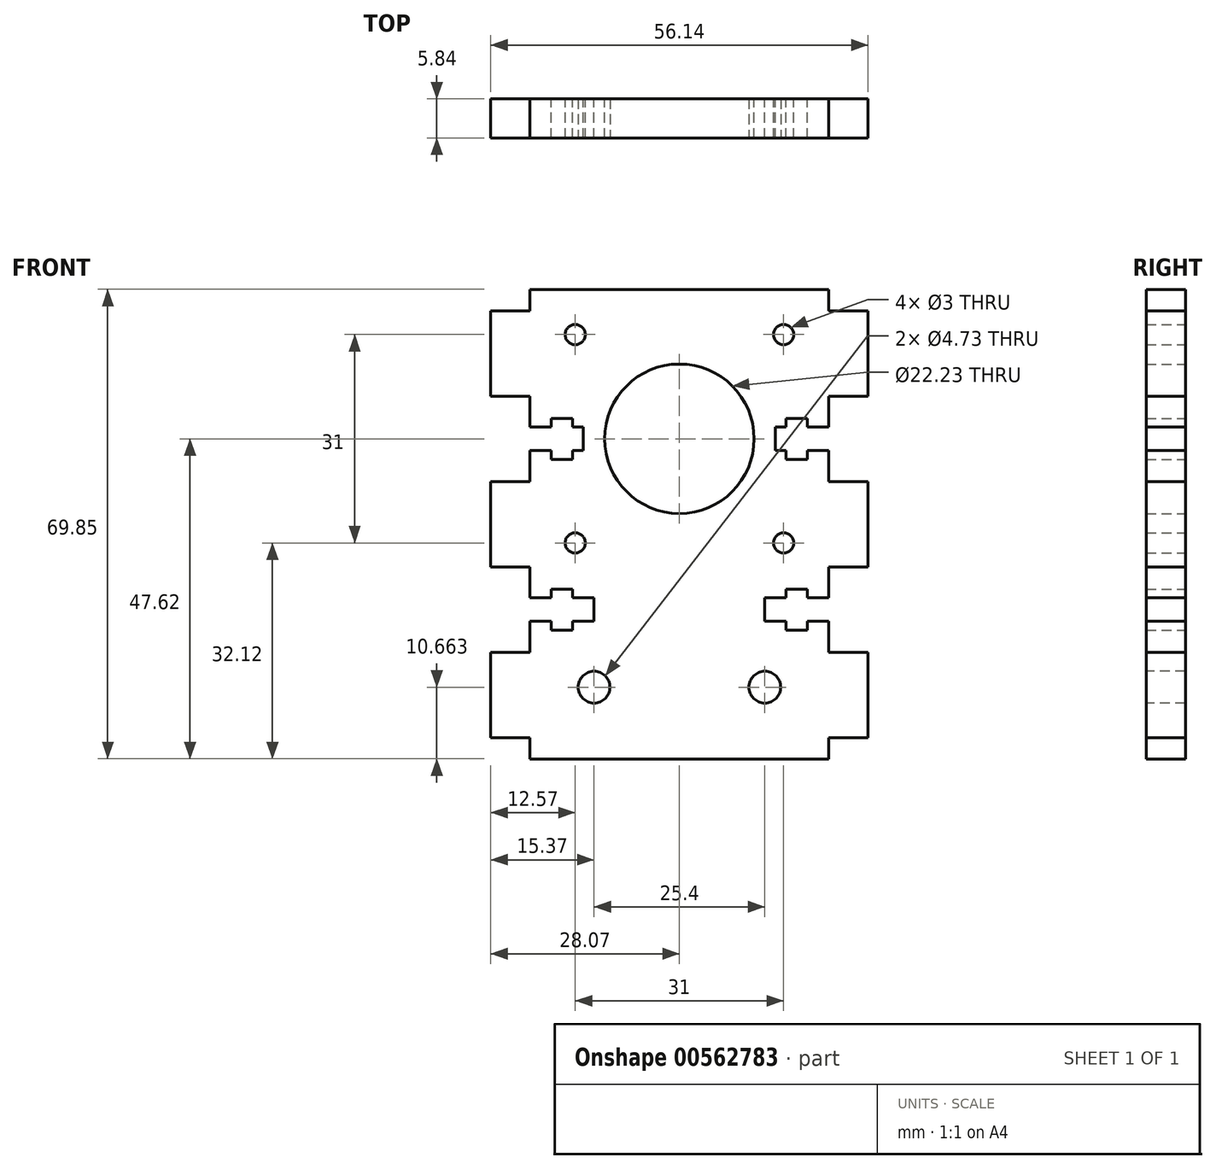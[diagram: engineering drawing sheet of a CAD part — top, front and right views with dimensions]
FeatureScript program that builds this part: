
annotation { "Feature Type Name" : "Feature", "Feature Type Description" : "" }
export const myFeature = defineFeature(function(context is Context, id is Id, definition is map)
    precondition{}
    {
        {
            var Q0;
            Q0=qCreatedBy(makeId("Front.planeOp"),FACE);
            var sketch = newSketch(context, id + "F0", { "sketchPlane" : qUnion([Q0])});
            skLineSegment(sketch, "E0.bottom", {"start": v(-22.22, 22.23) * mm, "end": v(22.23, 22.23) * mm});
            skLineSegment(sketch, "E0.top", {"start": v(-22.23, -22.23) * mm, "end": v(22.22, -22.23) * mm});
            skLineSegment(sketch, "E0.left", {"start": v(-22.22, 22.23) * mm, "end": v(-22.22, 19.05) * mm});
            skLineSegment(sketch, "E0.right", {"start": v(22.23, 22.23) * mm, "end": v(22.23, 19.05) * mm});
            skPoint(sketch, "E0.middle", {"position": v(0, 0) * mm});
            skLineSegment(sketch, "E1.bottom", {"start": v(-22.23, 6.35) * mm, "end": v(-28.07, 6.35) * mm});
            skLineSegment(sketch, "E1.top", {"start": v(-22.23, 19.05) * mm, "end": v(-28.07, 19.05) * mm});
            skLineSegment(sketch, "E1.right", {"start": v(-28.07, 6.35) * mm, "end": v(-28.07, 19.05) * mm});
            skPoint(sketch, "E1.middle", {"position": v(-25.15, 12.7) * mm});
            skLineSegment(sketch, "E2.MirrorCS", {"start": v(22.23, 19.05) * mm, "end": v(28.07, 19.05) * mm});
            skLineSegment(sketch, "E3.MirrorCS", {"start": v(28.07, 6.35) * mm, "end": v(28.07, 19.05) * mm});
            skLineSegment(sketch, "E4.MirrorCS", {"start": v(22.23, 6.35) * mm, "end": v(28.07, 6.35) * mm});
            skLineSegment(sketch, "E5.trimOffspring", {"start": v(-22.23, 6.35) * mm, "end": v(-22.23, 1.75) * mm});
            skLineSegment(sketch, "E6.trimOffspring", {"start": v(22.23, 6.35) * mm, "end": v(22.23, 1.75) * mm});
            skLineSegment(sketch, "E7.MirrorCS", {"start": v(-22.23, -19.05) * mm, "end": v(-28.07, -19.05) * mm});
            skLineSegment(sketch, "E8.MirrorCS", {"start": v(-28.07, -6.35) * mm, "end": v(-28.07, -19.05) * mm});
            skLineSegment(sketch, "E9.MirrorCS", {"start": v(-22.23, -6.35) * mm, "end": v(-28.07, -6.35) * mm});
            skLineSegment(sketch, "E10.MirrorCS", {"start": v(22.23, -6.35) * mm, "end": v(28.07, -6.35) * mm});
            skLineSegment(sketch, "E11.MirrorCS", {"start": v(28.07, -6.35) * mm, "end": v(28.07, -19.05) * mm});
            skLineSegment(sketch, "E12.MirrorCS", {"start": v(22.23, -19.05) * mm, "end": v(28.07, -19.05) * mm});
            skLineSegment(sketch, "E13.trimOffspring", {"start": v(-22.23, -19.05) * mm, "end": v(-22.23, -22.23) * mm});
            skLineSegment(sketch, "E14.trimOffspring", {"start": v(22.22, -19.05) * mm, "end": v(22.22, -22.23) * mm});
            skCircle(sketch, "E15", {"center": v(0, 0) * mm, "radius": 11.11 * mm});
            skCircle(sketch, "E16", {"center": v(15.5, 15.5) * mm, "radius": 1.5 * mm});
            skCircle(sketch, "E17.MirrorC", {"center": v(-15.5, 15.5) * mm, "radius": 1.5 * mm});
            skCircle(sketch, "E18.MirrorC", {"center": v(-15.5, -15.5) * mm, "radius": 1.5 * mm});
            skCircle(sketch, "E19.MirrorC", {"center": v(15.5, -15.5) * mm, "radius": 1.5 * mm});
            skLineSegment(sketch, "E20.bottom", {"start": v(-22.23, 1.75) * mm, "end": v(-19.05, 1.75) * mm});
            skLineSegment(sketch, "E20.top", {"start": v(-22.23, -1.75) * mm, "end": v(-19.05, -1.75) * mm});
            skPoint(sketch, "E20.middle", {"position": v(-20.64, 0) * mm});
            skLineSegment(sketch, "E21.bottom", {"start": v(-19.05, 3.05) * mm, "end": v(-15.88, 3.05) * mm});
            skLineSegment(sketch, "E21.top", {"start": v(-19.05, -3.05) * mm, "end": v(-15.88, -3.05) * mm});
            skLineSegment(sketch, "E21.left", {"start": v(-19.05, 3.05) * mm, "end": v(-19.05, 1.75) * mm});
            skLineSegment(sketch, "E21.right", {"start": v(-15.88, 3.05) * mm, "end": v(-15.88, 1.75) * mm});
            skPoint(sketch, "E21.middle", {"position": v(-17.46, 0) * mm});
            skLineSegment(sketch, "E22.bottom", {"start": v(-15.88, 1.75) * mm, "end": v(-14.29, 1.75) * mm});
            skLineSegment(sketch, "E22.top", {"start": v(-15.88, -1.75) * mm, "end": v(-14.29, -1.75) * mm});
            skLineSegment(sketch, "E22.right", {"start": v(-14.29, 1.75) * mm, "end": v(-14.29, -1.75) * mm});
            skPoint(sketch, "E22.middle", {"position": v(-15.08, 0) * mm});
            skLineSegment(sketch, "E23.trimOffspring", {"start": v(-19.05, -1.75) * mm, "end": v(-19.05, -3.05) * mm});
            skLineSegment(sketch, "E24.trimOffspring", {"start": v(-15.88, -1.75) * mm, "end": v(-15.88, -3.05) * mm});
            skLineSegment(sketch, "E25.trimOffspring", {"start": v(-22.23, -1.75) * mm, "end": v(-22.23, -6.35) * mm});
            skLineSegment(sketch, "E26.MirrorCS", {"start": v(15.88, 3.05) * mm, "end": v(15.88, 1.75) * mm});
            skLineSegment(sketch, "E27.MirrorCS", {"start": v(22.23, -1.75) * mm, "end": v(19.05, -1.75) * mm});
            skPoint(sketch, "E28.MirrorP", {"position": v(20.64, 0) * mm});
            skLineSegment(sketch, "E29.MirrorCS", {"start": v(19.05, 3.05) * mm, "end": v(15.88, 3.05) * mm});
            skLineSegment(sketch, "E30.MirrorCS", {"start": v(22.23, 1.75) * mm, "end": v(19.05, 1.75) * mm});
            skPoint(sketch, "E31.MirrorP", {"position": v(15.08, 0) * mm});
            skPoint(sketch, "E32.MirrorP", {"position": v(17.46, 0) * mm});
            skLineSegment(sketch, "E33.MirrorCS", {"start": v(19.05, 3.05) * mm, "end": v(19.05, 1.75) * mm});
            skLineSegment(sketch, "E34.MirrorCS", {"start": v(19.05, -1.75) * mm, "end": v(19.05, -3.05) * mm});
            skLineSegment(sketch, "E35.MirrorCS", {"start": v(15.88, 1.75) * mm, "end": v(14.29, 1.75) * mm});
            skLineSegment(sketch, "E36.MirrorCS", {"start": v(15.88, -1.75) * mm, "end": v(14.29, -1.75) * mm});
            skLineSegment(sketch, "E37.MirrorCS", {"start": v(15.88, -1.75) * mm, "end": v(15.88, -3.05) * mm});
            skLineSegment(sketch, "E38.MirrorCS", {"start": v(14.29, 1.75) * mm, "end": v(14.29, -1.75) * mm});
            skLineSegment(sketch, "E39.MirrorCS", {"start": v(19.05, -3.05) * mm, "end": v(15.88, -3.05) * mm});
            skLineSegment(sketch, "E40.MirrorCS", {"start": v(22.23, -1.75) * mm, "end": v(22.23, -6.35) * mm});
            skLineSegment(sketch, "E41.trimOffspring", {"start": v(22.23, -1.75) * mm, "end": v(22.22, -6.35) * mm});
            skSolve(sketch);
        }
        {
            var Q0;
            Q0 = qSketchRegion(id + "F0", true);
            extrude(context, id + "F1", {"entities" : qUnion([Q0]), "depth" : 5.84 * mm, "offsetDistance" : 25.4 * mm});
        }
        {
            var Q0;
            Q0=makeQuery(id+"F1.opExtrude","CAP_FACE",FACE,{"disambiguationData":[OSD([sQuery(id+"F0.wireOp",EDGE,"E0.bottom"),sQuery(id+"F0.wireOp",EDGE,"E0.top"),sQuery(id+"F0.wireOp",EDGE,"E0.left"),sQuery(id+"F0.wireOp",EDGE,"E0.right"),sQuery(id+"F0.wireOp",EDGE,"E1.bottom"),sQuery(id+"F0.wireOp",EDGE,"E1.top"),sQuery(id+"F0.wireOp",EDGE,"E1.right"),sQuery(id+"F0.wireOp",EDGE,"E2.MirrorCS"),sQuery(id+"F0.wireOp",EDGE,"E3.MirrorCS"),sQuery(id+"F0.wireOp",EDGE,"E4.MirrorCS"),sQuery(id+"F0.wireOp",EDGE,"E5.trimOffspring"),sQuery(id+"F0.wireOp",EDGE,"E7.MirrorCS"),sQuery(id+"F0.wireOp",EDGE,"E8.MirrorCS"),sQuery(id+"F0.wireOp",EDGE,"E9.MirrorCS"),sQuery(id+"F0.wireOp",EDGE,"E10.MirrorCS"),sQuery(id+"F0.wireOp",EDGE,"E11.MirrorCS"),sQuery(id+"F0.wireOp",EDGE,"E12.MirrorCS"),sQuery(id+"F0.wireOp",EDGE,"E13.trimOffspring"),sQuery(id+"F0.wireOp",EDGE,"E14.trimOffspring"),sQuery(id+"F0.wireOp",EDGE,"E15"),sQuery(id+"F0.wireOp",EDGE,"E16"),sQuery(id+"F0.wireOp",EDGE,"E17.MirrorC"),sQuery(id+"F0.wireOp",EDGE,"E18.MirrorC"),sQuery(id+"F0.wireOp",EDGE,"E19.MirrorC"),sQuery(id+"F0.wireOp",EDGE,"E20.bottom"),sQuery(id+"F0.wireOp",EDGE,"E20.top"),sQuery(id+"F0.wireOp",EDGE,"E21.bottom"),sQuery(id+"F0.wireOp",EDGE,"E21.top"),sQuery(id+"F0.wireOp",EDGE,"E21.left"),sQuery(id+"F0.wireOp",EDGE,"E21.right"),sQuery(id+"F0.wireOp",EDGE,"E22.bottom"),sQuery(id+"F0.wireOp",EDGE,"E22.top"),sQuery(id+"F0.wireOp",EDGE,"E22.right"),sQuery(id+"F0.wireOp",EDGE,"E23.trimOffspring"),sQuery(id+"F0.wireOp",EDGE,"E24.trimOffspring"),sQuery(id+"F0.wireOp",EDGE,"E25.trimOffspring"),sQuery(id+"F0.wireOp",EDGE,"E26.MirrorCS"),sQuery(id+"F0.wireOp",EDGE,"E27.MirrorCS"),sQuery(id+"F0.wireOp",EDGE,"E29.MirrorCS"),sQuery(id+"F0.wireOp",EDGE,"E30.MirrorCS"),sQuery(id+"F0.wireOp",EDGE,"E33.MirrorCS"),sQuery(id+"F0.wireOp",EDGE,"E6.trimOffspring"),sQuery(id+"F0.wireOp",EDGE,"E34.MirrorCS"),sQuery(id+"F0.wireOp",EDGE,"E35.MirrorCS"),sQuery(id+"F0.wireOp",EDGE,"E36.MirrorCS"),sQuery(id+"F0.wireOp",EDGE,"E37.MirrorCS"),sQuery(id+"F0.wireOp",EDGE,"E38.MirrorCS"),sQuery(id+"F0.wireOp",EDGE,"E39.MirrorCS"),sQuery(id+"F0.wireOp",EDGE,"E41.trimOffspring")])],"isStart":false});
            var sketch = newSketch(context, id + "F2", { "sketchPlane" : qUnion([Q0])});
            skLineSegment(sketch, "E42.bottom", {"start": v(-22.23, -22.23) * mm, "end": v(22.23, -22.23) * mm});
            skLineSegment(sketch, "E42.top", {"start": v(-22.23, -47.62) * mm, "end": v(22.23, -47.62) * mm});
            skLineSegment(sketch, "E42.left", {"start": v(-22.23, -22.23) * mm, "end": v(-22.23, -31.75) * mm});
            skLineSegment(sketch, "E42.right", {"start": v(22.23, -22.23) * mm, "end": v(22.23, -31.75) * mm});
            skPoint(sketch, "E42.middle", {"position": v(0, -34.92) * mm});
            skLineSegment(sketch, "E43.bottom", {"start": v(-22.23, -31.75) * mm, "end": v(-28.07, -31.75) * mm});
            skLineSegment(sketch, "E43.top", {"start": v(-22.23, -44.45) * mm, "end": v(-28.07, -44.45) * mm});
            skLineSegment(sketch, "E43.right", {"start": v(-28.07, -31.75) * mm, "end": v(-28.07, -44.45) * mm});
            skPoint(sketch, "E43.middle", {"position": v(-25.15, -38.1) * mm});
            skLineSegment(sketch, "E44", {"start": v(-28.07, -12.7) * mm, "end": v(28.07, -12.7) * mm, "construction": true});
            skLineSegment(sketch, "E45.trimOffspring", {"start": v(-22.23, -44.45) * mm, "end": v(-22.23, -47.62) * mm});
            skLineSegment(sketch, "E46.MirrorCS", {"start": v(22.23, -31.75) * mm, "end": v(28.07, -31.75) * mm});
            skLineSegment(sketch, "E47.MirrorCS", {"start": v(28.07, -31.75) * mm, "end": v(28.07, -44.45) * mm});
            skPoint(sketch, "E48.MirrorP", {"position": v(25.15, -38.1) * mm});
            skLineSegment(sketch, "E49.MirrorCS", {"start": v(22.23, -44.45) * mm, "end": v(28.07, -44.45) * mm});
            skLineSegment(sketch, "E50.trimOffspring", {"start": v(22.23, -44.45) * mm, "end": v(22.23, -47.62) * mm});
            skSolve(sketch);
        }
        {
            var Q0;
            Q0 = qSketchRegion(id + "F2", true);
            var Q1;
            Q1=makeQuery(id+"F1.opExtrude","CAP_FACE",FACE,{"disambiguationData":[OSD([sQuery(id+"F0.wireOp",EDGE,"E0.bottom"),sQuery(id+"F0.wireOp",EDGE,"E0.top"),sQuery(id+"F0.wireOp",EDGE,"E0.left"),sQuery(id+"F0.wireOp",EDGE,"E0.right"),sQuery(id+"F0.wireOp",EDGE,"E1.bottom"),sQuery(id+"F0.wireOp",EDGE,"E1.top"),sQuery(id+"F0.wireOp",EDGE,"E1.right"),sQuery(id+"F0.wireOp",EDGE,"E2.MirrorCS"),sQuery(id+"F0.wireOp",EDGE,"E3.MirrorCS"),sQuery(id+"F0.wireOp",EDGE,"E4.MirrorCS"),sQuery(id+"F0.wireOp",EDGE,"E5.trimOffspring"),sQuery(id+"F0.wireOp",EDGE,"E7.MirrorCS"),sQuery(id+"F0.wireOp",EDGE,"E8.MirrorCS"),sQuery(id+"F0.wireOp",EDGE,"E9.MirrorCS"),sQuery(id+"F0.wireOp",EDGE,"E10.MirrorCS"),sQuery(id+"F0.wireOp",EDGE,"E11.MirrorCS"),sQuery(id+"F0.wireOp",EDGE,"E12.MirrorCS"),sQuery(id+"F0.wireOp",EDGE,"E13.trimOffspring"),sQuery(id+"F0.wireOp",EDGE,"E14.trimOffspring"),sQuery(id+"F0.wireOp",EDGE,"E15"),sQuery(id+"F0.wireOp",EDGE,"E16"),sQuery(id+"F0.wireOp",EDGE,"E17.MirrorC"),sQuery(id+"F0.wireOp",EDGE,"E18.MirrorC"),sQuery(id+"F0.wireOp",EDGE,"E19.MirrorC"),sQuery(id+"F0.wireOp",EDGE,"E20.bottom"),sQuery(id+"F0.wireOp",EDGE,"E20.top"),sQuery(id+"F0.wireOp",EDGE,"E21.bottom"),sQuery(id+"F0.wireOp",EDGE,"E21.top"),sQuery(id+"F0.wireOp",EDGE,"E21.left"),sQuery(id+"F0.wireOp",EDGE,"E21.right"),sQuery(id+"F0.wireOp",EDGE,"E22.bottom"),sQuery(id+"F0.wireOp",EDGE,"E22.top"),sQuery(id+"F0.wireOp",EDGE,"E22.right"),sQuery(id+"F0.wireOp",EDGE,"E23.trimOffspring"),sQuery(id+"F0.wireOp",EDGE,"E24.trimOffspring"),sQuery(id+"F0.wireOp",EDGE,"E25.trimOffspring"),sQuery(id+"F0.wireOp",EDGE,"E26.MirrorCS"),sQuery(id+"F0.wireOp",EDGE,"E27.MirrorCS"),sQuery(id+"F0.wireOp",EDGE,"E29.MirrorCS"),sQuery(id+"F0.wireOp",EDGE,"E30.MirrorCS"),sQuery(id+"F0.wireOp",EDGE,"E33.MirrorCS"),sQuery(id+"F0.wireOp",EDGE,"E6.trimOffspring"),sQuery(id+"F0.wireOp",EDGE,"E34.MirrorCS"),sQuery(id+"F0.wireOp",EDGE,"E35.MirrorCS"),sQuery(id+"F0.wireOp",EDGE,"E36.MirrorCS"),sQuery(id+"F0.wireOp",EDGE,"E37.MirrorCS"),sQuery(id+"F0.wireOp",EDGE,"E38.MirrorCS"),sQuery(id+"F0.wireOp",EDGE,"E39.MirrorCS"),sQuery(id+"F0.wireOp",EDGE,"E41.trimOffspring")])],"isStart":true});
            extrude(context, id + "F3", {"entities" : qUnion([Q0]), "operationType" : NewBodyOperationType.ADD, "endBound" : BoundingType.UP_TO_SURFACE, "oppositeDirection" : true, "depth" : 25.4 * mm, "endBoundEntityFace" : qUnion([Q1]), "offsetDistance" : 25.4 * mm});
        }
        {
            var Q0;
            {var subQ0=sQuery(id+"F0.wireOp",EDGE,"E41.trimOffspring");var subQ1=sQuery(id+"F0.wireOp",EDGE,"E39.MirrorCS");var subQ2=sQuery(id+"F0.wireOp",EDGE,"E38.MirrorCS");var subQ3=sQuery(id+"F0.wireOp",EDGE,"E37.MirrorCS");var subQ4=sQuery(id+"F0.wireOp",EDGE,"E36.MirrorCS");var subQ5=sQuery(id+"F0.wireOp",EDGE,"E35.MirrorCS");var subQ6=sQuery(id+"F0.wireOp",EDGE,"E34.MirrorCS");var subQ7=sQuery(id+"F0.wireOp",EDGE,"E6.trimOffspring");var subQ8=sQuery(id+"F0.wireOp",EDGE,"E33.MirrorCS");var subQ9=sQuery(id+"F0.wireOp",EDGE,"E30.MirrorCS");var subQ10=sQuery(id+"F0.wireOp",EDGE,"E29.MirrorCS");var subQ11=sQuery(id+"F0.wireOp",EDGE,"E27.MirrorCS");var subQ12=sQuery(id+"F0.wireOp",EDGE,"E26.MirrorCS");var subQ13=sQuery(id+"F0.wireOp",EDGE,"E25.trimOffspring");var subQ14=sQuery(id+"F0.wireOp",EDGE,"E24.trimOffspring");var subQ15=sQuery(id+"F0.wireOp",EDGE,"E23.trimOffspring");var subQ16=sQuery(id+"F0.wireOp",EDGE,"E22.right");var subQ17=sQuery(id+"F0.wireOp",EDGE,"E22.top");var subQ18=sQuery(id+"F0.wireOp",EDGE,"E22.bottom");var subQ19=sQuery(id+"F0.wireOp",EDGE,"E21.right");var subQ20=sQuery(id+"F0.wireOp",EDGE,"E21.left");var subQ21=sQuery(id+"F0.wireOp",EDGE,"E21.top");var subQ22=sQuery(id+"F0.wireOp",EDGE,"E21.bottom");var subQ23=sQuery(id+"F0.wireOp",EDGE,"E20.top");var subQ24=sQuery(id+"F0.wireOp",EDGE,"E20.bottom");var subQ25=sQuery(id+"F0.wireOp",EDGE,"E19.MirrorC");var subQ26=sQuery(id+"F0.wireOp",EDGE,"E18.MirrorC");var subQ27=sQuery(id+"F0.wireOp",EDGE,"E17.MirrorC");var subQ28=sQuery(id+"F0.wireOp",EDGE,"E16");var subQ29=sQuery(id+"F0.wireOp",EDGE,"E15");var subQ30=sQuery(id+"F0.wireOp",EDGE,"E14.trimOffspring");var subQ31=sQuery(id+"F0.wireOp",EDGE,"E13.trimOffspring");var subQ32=sQuery(id+"F0.wireOp",EDGE,"E12.MirrorCS");var subQ33=sQuery(id+"F0.wireOp",EDGE,"E11.MirrorCS");var subQ34=sQuery(id+"F0.wireOp",EDGE,"E10.MirrorCS");var subQ35=sQuery(id+"F0.wireOp",EDGE,"E9.MirrorCS");var subQ36=sQuery(id+"F0.wireOp",EDGE,"E8.MirrorCS");var subQ37=sQuery(id+"F0.wireOp",EDGE,"E7.MirrorCS");var subQ38=sQuery(id+"F0.wireOp",EDGE,"E5.trimOffspring");var subQ39=sQuery(id+"F0.wireOp",EDGE,"E4.MirrorCS");var subQ40=sQuery(id+"F0.wireOp",EDGE,"E3.MirrorCS");var subQ41=sQuery(id+"F0.wireOp",EDGE,"E2.MirrorCS");var subQ42=sQuery(id+"F0.wireOp",EDGE,"E1.right");var subQ43=sQuery(id+"F0.wireOp",EDGE,"E1.top");var subQ44=sQuery(id+"F0.wireOp",EDGE,"E1.bottom");var subQ45=sQuery(id+"F0.wireOp",EDGE,"E0.right");var subQ46=sQuery(id+"F0.wireOp",EDGE,"E0.left");var subQ47=sQuery(id+"F0.wireOp",EDGE,"E0.top");var subQ48=sQuery(id+"F0.wireOp",EDGE,"E0.bottom");Q0=makeQuery(id+"F3.boolean.opBoolean","MERGE",FACE,{"derivedFrom":[makeQuery(id+"F1.opExtrude","CAP_FACE",FACE,{"disambiguationData":[OSD([subQ48,subQ47,subQ46,subQ45,subQ44,subQ43,subQ42,subQ41,subQ40,subQ39,subQ38,subQ37,subQ36,subQ35,subQ34,subQ33,subQ32,subQ31,subQ30,subQ29,subQ28,subQ27,subQ26,subQ25,subQ24,subQ23,subQ22,subQ21,subQ20,subQ19,subQ18,subQ17,subQ16,subQ15,subQ14,subQ13,subQ12,subQ11,subQ10,subQ9,subQ8,subQ7,subQ6,subQ5,subQ4,subQ3,subQ2,subQ1,subQ0])],"isStart":true}),makeQuery(id+"F3.opExtrude","CAP_FACE",FACE,{"disambiguationData":[OSD([subQ48,subQ47,subQ46,subQ45,subQ44,subQ43,subQ42,subQ41,subQ40,subQ39,subQ38,subQ37,subQ36,subQ35,subQ34,subQ33,subQ32,subQ31,subQ30,subQ29,subQ28,subQ27,subQ26,subQ25,subQ24,subQ23,subQ22,subQ21,subQ20,subQ19,subQ18,subQ17,subQ16,subQ15,subQ14,subQ13,subQ12,subQ11,subQ10,subQ9,subQ8,subQ7,subQ6,subQ5,subQ4,subQ3,subQ2,subQ1,subQ0])],"isStart":false})]});}
            var sketch = newSketch(context, id + "F4", { "sketchPlane" : qUnion([Q0])});
            skLineSegment(sketch, "E51", {"start": v(22.23, -25.4) * mm, "end": v(-22.22, -25.4) * mm, "construction": true});
            skLineSegment(sketch, "E52.bottom", {"start": v(22.23, -23.65) * mm, "end": v(19.05, -23.65) * mm});
            skLineSegment(sketch, "E52.top", {"start": v(22.23, -27.15) * mm, "end": v(19.05, -27.15) * mm});
            skLineSegment(sketch, "E52.left", {"start": v(22.23, -23.65) * mm, "end": v(22.23, -27.15) * mm});
            skPoint(sketch, "E52.middle", {"position": v(20.64, -25.4) * mm});
            skLineSegment(sketch, "E53.bottom", {"start": v(19.05, -22.35) * mm, "end": v(15.88, -22.35) * mm});
            skLineSegment(sketch, "E53.top", {"start": v(19.05, -28.45) * mm, "end": v(15.88, -28.45) * mm});
            skLineSegment(sketch, "E53.left", {"start": v(19.05, -22.35) * mm, "end": v(19.05, -23.65) * mm});
            skLineSegment(sketch, "E53.right", {"start": v(15.88, -22.35) * mm, "end": v(15.88, -23.65) * mm});
            skPoint(sketch, "E53.middle", {"position": v(17.46, -25.4) * mm});
            skLineSegment(sketch, "E54.bottom", {"start": v(15.88, -23.65) * mm, "end": v(12.7, -23.65) * mm});
            skLineSegment(sketch, "E54.top", {"start": v(15.88, -27.15) * mm, "end": v(12.7, -27.15) * mm});
            skLineSegment(sketch, "E54.right", {"start": v(12.7, -23.65) * mm, "end": v(12.7, -27.15) * mm});
            skPoint(sketch, "E54.middle", {"position": v(14.29, -25.4) * mm});
            skLineSegment(sketch, "E55.trimOffspring", {"start": v(15.88, -27.15) * mm, "end": v(15.88, -28.45) * mm});
            skLineSegment(sketch, "E56.trimOffspring", {"start": v(19.05, -27.15) * mm, "end": v(19.05, -28.45) * mm});
            skLineSegment(sketch, "E57.MirrorCS", {"start": v(-19.05, -27.15) * mm, "end": v(-19.05, -28.45) * mm});
            skLineSegment(sketch, "E58.MirrorCS", {"start": v(-15.88, -27.15) * mm, "end": v(-15.88, -28.45) * mm});
            skLineSegment(sketch, "E59.MirrorCS", {"start": v(-19.05, -22.35) * mm, "end": v(-19.05, -23.65) * mm});
            skLineSegment(sketch, "E60.MirrorCS", {"start": v(-15.88, -22.35) * mm, "end": v(-15.88, -23.65) * mm});
            skLineSegment(sketch, "E61.MirrorCS", {"start": v(-22.23, -23.65) * mm, "end": v(-22.23, -27.15) * mm});
            skPoint(sketch, "E62.MirrorP", {"position": v(-17.46, -25.4) * mm});
            skPoint(sketch, "E63.MirrorP", {"position": v(-14.29, -25.4) * mm});
            skPoint(sketch, "E64.MirrorP", {"position": v(-20.64, -25.4) * mm});
            skLineSegment(sketch, "E65.MirrorCS", {"start": v(-12.7, -23.65) * mm, "end": v(-12.7, -27.15) * mm});
            skLineSegment(sketch, "E66.MirrorCS", {"start": v(-22.23, -23.65) * mm, "end": v(-19.05, -23.65) * mm});
            skLineSegment(sketch, "E67.MirrorCS", {"start": v(-22.23, -27.15) * mm, "end": v(-19.05, -27.15) * mm});
            skLineSegment(sketch, "E68.MirrorCS", {"start": v(-22.23, -25.4) * mm, "end": v(22.22, -25.4) * mm, "construction": true});
            skLineSegment(sketch, "E69.MirrorCS", {"start": v(-19.05, -22.35) * mm, "end": v(-15.88, -22.35) * mm});
            skLineSegment(sketch, "E70.MirrorCS", {"start": v(-19.05, -28.45) * mm, "end": v(-15.88, -28.45) * mm});
            skLineSegment(sketch, "E71.MirrorCS", {"start": v(-15.88, -27.15) * mm, "end": v(-12.7, -27.15) * mm});
            skLineSegment(sketch, "E72.MirrorCS", {"start": v(-15.88, -23.65) * mm, "end": v(-12.7, -23.65) * mm});
            skSolve(sketch);
        }
        {
            var Q0;
            Q0 = qSketchRegion(id + "F4", true);
            extrude(context, id + "F5", {"entities" : qUnion([Q0]), "operationType" : NewBodyOperationType.REMOVE, "oppositeDirection" : true, "depth" : 25.4 * mm, "offsetDistance" : 25.4 * mm});
        }
        {
            var Q0;
            Q0=makeQuery(id+"F3.boolean.opBoolean","MERGE",FACE,{"derivedFrom":[makeQuery(id+"F1.opExtrude","CAP_FACE",FACE,{"disambiguationData":[OSD([sQuery(id+"F0.wireOp",EDGE,"E0.bottom"),sQuery(id+"F0.wireOp",EDGE,"E0.top"),sQuery(id+"F0.wireOp",EDGE,"E0.left"),sQuery(id+"F0.wireOp",EDGE,"E0.right"),sQuery(id+"F0.wireOp",EDGE,"E1.bottom"),sQuery(id+"F0.wireOp",EDGE,"E1.top"),sQuery(id+"F0.wireOp",EDGE,"E1.right"),sQuery(id+"F0.wireOp",EDGE,"E2.MirrorCS"),sQuery(id+"F0.wireOp",EDGE,"E3.MirrorCS"),sQuery(id+"F0.wireOp",EDGE,"E4.MirrorCS"),sQuery(id+"F0.wireOp",EDGE,"E5.trimOffspring"),sQuery(id+"F0.wireOp",EDGE,"E7.MirrorCS"),sQuery(id+"F0.wireOp",EDGE,"E8.MirrorCS"),sQuery(id+"F0.wireOp",EDGE,"E9.MirrorCS"),sQuery(id+"F0.wireOp",EDGE,"E10.MirrorCS"),sQuery(id+"F0.wireOp",EDGE,"E11.MirrorCS"),sQuery(id+"F0.wireOp",EDGE,"E12.MirrorCS"),sQuery(id+"F0.wireOp",EDGE,"E13.trimOffspring"),sQuery(id+"F0.wireOp",EDGE,"E14.trimOffspring"),sQuery(id+"F0.wireOp",EDGE,"E15"),sQuery(id+"F0.wireOp",EDGE,"E16"),sQuery(id+"F0.wireOp",EDGE,"E17.MirrorC"),sQuery(id+"F0.wireOp",EDGE,"E18.MirrorC"),sQuery(id+"F0.wireOp",EDGE,"E19.MirrorC"),sQuery(id+"F0.wireOp",EDGE,"E20.bottom"),sQuery(id+"F0.wireOp",EDGE,"E20.top"),sQuery(id+"F0.wireOp",EDGE,"E21.bottom"),sQuery(id+"F0.wireOp",EDGE,"E21.top"),sQuery(id+"F0.wireOp",EDGE,"E21.left"),sQuery(id+"F0.wireOp",EDGE,"E21.right"),sQuery(id+"F0.wireOp",EDGE,"E22.bottom"),sQuery(id+"F0.wireOp",EDGE,"E22.top"),sQuery(id+"F0.wireOp",EDGE,"E22.right"),sQuery(id+"F0.wireOp",EDGE,"E23.trimOffspring"),sQuery(id+"F0.wireOp",EDGE,"E24.trimOffspring"),sQuery(id+"F0.wireOp",EDGE,"E25.trimOffspring"),sQuery(id+"F0.wireOp",EDGE,"E26.MirrorCS"),sQuery(id+"F0.wireOp",EDGE,"E27.MirrorCS"),sQuery(id+"F0.wireOp",EDGE,"E29.MirrorCS"),sQuery(id+"F0.wireOp",EDGE,"E30.MirrorCS"),sQuery(id+"F0.wireOp",EDGE,"E33.MirrorCS"),sQuery(id+"F0.wireOp",EDGE,"E6.trimOffspring"),sQuery(id+"F0.wireOp",EDGE,"E34.MirrorCS"),sQuery(id+"F0.wireOp",EDGE,"E35.MirrorCS"),sQuery(id+"F0.wireOp",EDGE,"E36.MirrorCS"),sQuery(id+"F0.wireOp",EDGE,"E37.MirrorCS"),sQuery(id+"F0.wireOp",EDGE,"E38.MirrorCS"),sQuery(id+"F0.wireOp",EDGE,"E39.MirrorCS"),sQuery(id+"F0.wireOp",EDGE,"E41.trimOffspring")])],"isStart":false}),makeQuery(id+"F3.opExtrude","CAP_FACE",FACE,{"disambiguationData":[OSD([sQuery(id+"F2.wireOp",EDGE,"E42.bottom"),sQuery(id+"F2.wireOp",EDGE,"E42.top"),sQuery(id+"F2.wireOp",EDGE,"E42.left"),sQuery(id+"F2.wireOp",EDGE,"E42.right"),sQuery(id+"F2.wireOp",EDGE,"E43.bottom"),sQuery(id+"F2.wireOp",EDGE,"E43.top"),sQuery(id+"F2.wireOp",EDGE,"E43.right"),sQuery(id+"F2.wireOp",EDGE,"E45.trimOffspring"),sQuery(id+"F2.wireOp",EDGE,"E46.MirrorCS"),sQuery(id+"F2.wireOp",EDGE,"E47.MirrorCS"),sQuery(id+"F2.wireOp",EDGE,"E49.MirrorCS"),sQuery(id+"F2.wireOp",EDGE,"E50.trimOffspring")])],"isStart":true})]});
            var sketch = newSketch(context, id + "F6", { "sketchPlane" : qUnion([Q0])});
            skLineSegment(sketch, "E73", {"start": v(0, 22.22) * mm, "end": v(0, -47.62) * mm, "construction": true});
            skCircle(sketch, "E74", {"center": v(-12.7, -36.96) * mm, "radius": 2.36 * mm});
            skCircle(sketch, "E75.MirrorC", {"center": v(12.7, -36.96) * mm, "radius": 2.36 * mm});
            skSolve(sketch);
        }
        {
            var Q0;
            Q0 = qSketchRegion(id + "F6", true);
            extrude(context, id + "F7", {"entities" : qUnion([Q0]), "operationType" : NewBodyOperationType.REMOVE, "oppositeDirection" : true, "depth" : 25.4 * mm, "offsetDistance" : 25.4 * mm});
        }
    });
